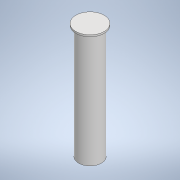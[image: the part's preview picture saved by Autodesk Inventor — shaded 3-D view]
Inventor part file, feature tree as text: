
AUTODESK INVENTOR PART (.ipt)
format: ipt  version: 2022 (Build 260153000, 153)  size: 102,912 bytes
history: native  units: mm
features: extrude x2, sketch x2
ambient origin geometry x8: Origin, YZ Plane, XZ Plane, XY Plane, X Axis, Y Axis, Z Axis, Center Point
bodies: Solid1 (feature_tree)
feature tree (4):
  extrude  "Extrusion1"  Depth=99.9mm TaperAngle=0.0deg
  extrude  "Extrusion2"  Depth=1.5mm TaperAngle=0.0deg
  sketch  "Sketch1"  dims[d0=20.0mm d1=99.9mm d2=0.0mm]
  sketch  "Sketch2"  dims[d3=24.8mm d4=1.5mm d5=0.0mm]
